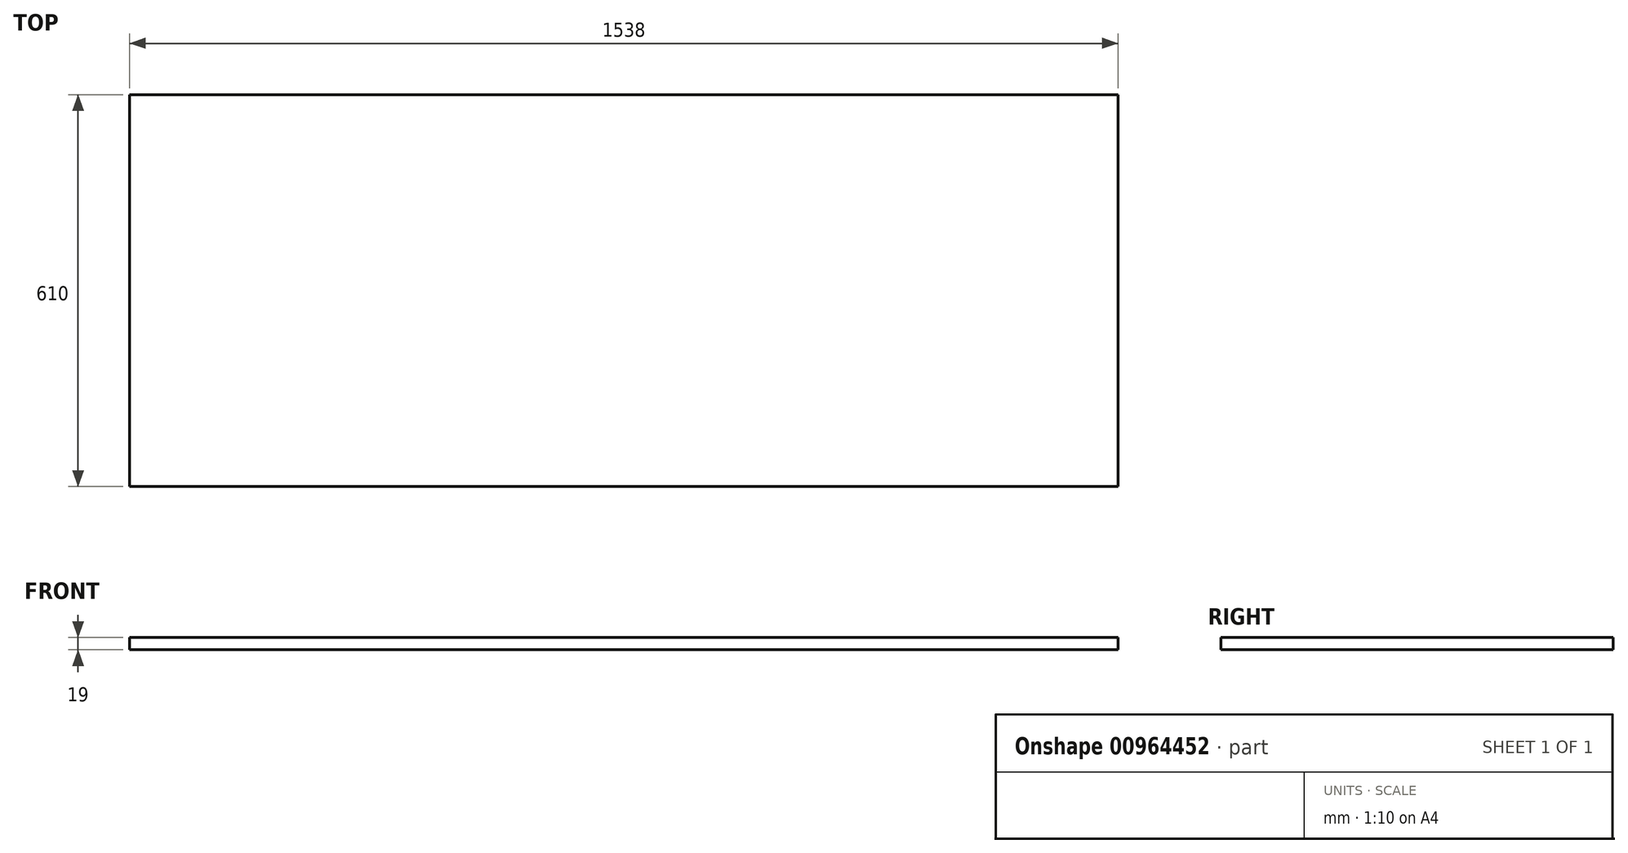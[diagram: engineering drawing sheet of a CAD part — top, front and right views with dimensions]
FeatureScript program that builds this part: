
annotation { "Feature Type Name" : "Feature", "Feature Type Description" : "" }
export const myFeature = defineFeature(function(context is Context, id is Id, definition is map)
    precondition{}
    {
        {
            var Q0;
            Q0=qCreatedBy(makeId("Top.planeOp"),FACE);
            var sketch = newSketch(context, id + "F0", { "sketchPlane" : qUnion([Q0])});
            skLineSegment(sketch, "E0.bottom", {"start": v(0, 0) * mm, "end": v(1538, 0) * mm});
            skLineSegment(sketch, "E0.top", {"start": v(0, 610) * mm, "end": v(1538, 610) * mm});
            skLineSegment(sketch, "E0.left", {"start": v(0, 0) * mm, "end": v(0, 610) * mm});
            skLineSegment(sketch, "E0.right", {"start": v(1538, 0) * mm, "end": v(1538, 610) * mm});
            skSolve(sketch);
        }
        {
            var Q0;
            Q0=qSketchRegion(id+"F0",true);
            extrude(context, id + "F1", {"entities" : qUnion([Q0]), "depth" : 19 * mm, "offsetDistance" : 25 * mm});
        }
    });
